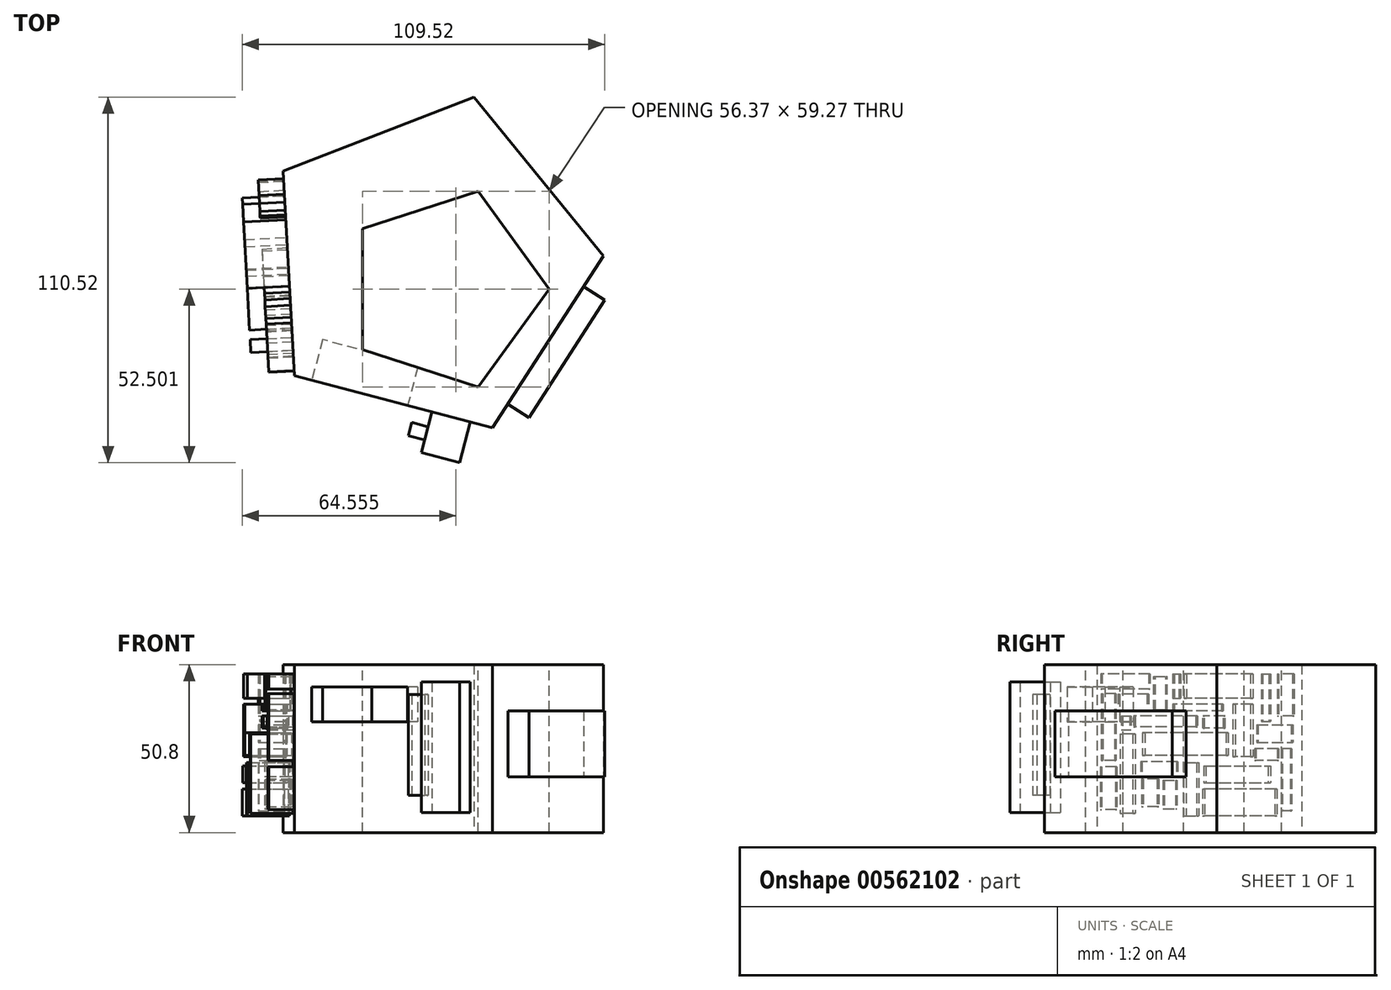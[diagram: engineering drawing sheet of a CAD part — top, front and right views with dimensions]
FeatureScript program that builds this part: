
annotation { "Feature Type Name" : "Feature", "Feature Type Description" : "" }
export const myFeature = defineFeature(function(context is Context, id is Id, definition is map)
    precondition{}
    {
        {
            var Q0;
            Q0=qCreatedBy(makeId("Top.planeOp"),FACE);
            var sketch = newSketch(context, id + "F0", { "sketchPlane" : qUnion([Q0])});
            skCircle(sketch, "E0.cCircle", {"center": v(-35.8, 17.43) * mm, "radius": 42.6 * mm, "construction": true});
            skLineSegment(sketch, "E0.0", {"start": v(16.77, 20.35) * mm, "end": v(-16.77, -31.67) * mm});
            skLineSegment(sketch, "E0.1", {"start": v(-16.77, -31.67) * mm, "end": v(-76.61, -15.84) * mm});
            skLineSegment(sketch, "E0.2", {"start": v(-76.61, -15.84) * mm, "end": v(-80.05, 45.96) * mm});
            skLineSegment(sketch, "E0.3", {"start": v(-80.05, 45.96) * mm, "end": v(-22.34, 68.33) * mm});
            skLineSegment(sketch, "E0.4", {"start": v(-22.34, 68.33) * mm, "end": v(16.77, 20.35) * mm});
            skPoint(sketch, "E0.0.midPoint", {"position": v(0, -5.66) * mm});
            skSolve(sketch);
        }
        {
            var Q0;
            Q0 = qSketchRegion(id + "F0", true);
            extrude(context, id + "F1", {"entities" : qUnion([Q0]), "depth" : 25.4 * mm, "offsetDistance" : 25.4 * mm});
        }
        {
            var Q0;
            Q0=makeQuery(id+"F1.opExtrude","CAP_FACE",FACE,{"disambiguationData":[OSD([sQuery(id+"F0.wireOp",EDGE,"E0.0"),sQuery(id+"F0.wireOp",EDGE,"E0.1"),sQuery(id+"F0.wireOp",EDGE,"E0.2"),sQuery(id+"F0.wireOp",EDGE,"E0.3"),sQuery(id+"F0.wireOp",EDGE,"E0.4")])],"isStart":true});
            extrude(context, id + "F2", {"entities" : qUnion([Q0]), "operationType" : NewBodyOperationType.ADD, "depth" : 25.4 * mm, "offsetDistance" : 25.4 * mm});
        }
        {
            var Q0;
            {var subQ0=sQuery(id+"F0.wireOp",EDGE,"E0.0");Q0=makeQuery(id+"F2.boolean.opBoolean","MERGE",FACE,{"derivedFrom":[makeQuery(id+"F1.opExtrude","SWEPT_FACE",FACE,{"disambiguationData":[OSD([subQ0])]}),makeQuery(id+"F2.opExtrude","SWEPT_FACE",FACE,{"disambiguationData":[OSD([subQ0])]})]});}
            var sketch = newSketch(context, id + "F3", { "sketchPlane" : qUnion([Q0])});
            skLineSegment(sketch, "E1.bottom", {"start": v(-27.1, 11.35) * mm, "end": v(15.17, 11.35) * mm});
            skLineSegment(sketch, "E1.top", {"start": v(-27.1, -8.59) * mm, "end": v(15.17, -8.59) * mm});
            skLineSegment(sketch, "E1.left", {"start": v(-27.1, 11.35) * mm, "end": v(-27.1, -8.59) * mm});
            skLineSegment(sketch, "E1.right", {"start": v(15.17, 11.35) * mm, "end": v(15.17, -8.59) * mm});
            skSolve(sketch);
        }
        {
            var Q0;
            Q0 = qSketchRegion(id + "F3", true);
            extrude(context, id + "F4", {"entities" : qUnion([Q0]), "operationType" : NewBodyOperationType.ADD, "depth" : 7.62 * mm, "offsetDistance" : 25.4 * mm});
        }
        {
            var Q0;
            {var subQ0=sQuery(id+"F0.wireOp",EDGE,"E0.1");Q0=makeQuery(id+"F2.boolean.opBoolean","MERGE",FACE,{"derivedFrom":[makeQuery(id+"F1.opExtrude","SWEPT_FACE",FACE,{"disambiguationData":[OSD([subQ0])]}),makeQuery(id+"F2.opExtrude","SWEPT_FACE",FACE,{"disambiguationData":[OSD([subQ0])]})]});}
            var sketch = newSketch(context, id + "F5", { "sketchPlane" : qUnion([Q0])});
            skLineSegment(sketch, "E2.bottom", {"start": v(-15, 20.12) * mm, "end": v(-26.99, 20.12) * mm});
            skLineSegment(sketch, "E2.top", {"start": v(-15, -19.39) * mm, "end": v(-26.99, -19.39) * mm});
            skLineSegment(sketch, "E2.left", {"start": v(-15, 20.12) * mm, "end": v(-15, -19.39) * mm});
            skLineSegment(sketch, "E2.right", {"start": v(-26.99, 20.12) * mm, "end": v(-26.99, -19.39) * mm});
            skSolve(sketch);
        }
        {
            var Q0;
            Q0 = qSketchRegion(id + "F5", true);
            extrude(context, id + "F6", {"entities" : qUnion([Q0]), "operationType" : NewBodyOperationType.ADD, "depth" : 12.7 * mm, "offsetDistance" : 25.4 * mm});
        }
        {
            var Q0;
            {var subQ0=sQuery(id+"F0.wireOp",EDGE,"E0.1");Q0=makeQuery(id+"F2.boolean.opBoolean","MERGE",FACE,{"derivedFrom":[makeQuery(id+"F1.opExtrude","SWEPT_FACE",FACE,{"disambiguationData":[OSD([subQ0])]}),makeQuery(id+"F2.opExtrude","SWEPT_FACE",FACE,{"disambiguationData":[OSD([subQ0])]})]});}
            var sketch = newSketch(context, id + "F7", { "sketchPlane" : qUnion([Q0])});
            skLineSegment(sketch, "E3.bottom", {"start": v(-32.68, 7.96) * mm, "end": v(-63.89, 7.96) * mm});
            skLineSegment(sketch, "E3.top", {"start": v(-32.68, 19.19) * mm, "end": v(-63.89, 19.19) * mm});
            skLineSegment(sketch, "E3.left", {"start": v(-32.68, 7.96) * mm, "end": v(-32.68, 19.19) * mm});
            skLineSegment(sketch, "E3.right", {"start": v(-63.89, 7.96) * mm, "end": v(-63.89, 19.19) * mm});
            skSolve(sketch);
        }
        {
            var Q0;
            Q0=makeQuery(id+"F7.imprint","IMPRINT",FACE,{"disambiguationData":[TD([[makeQuery(id+"F7.imprint","IMPRINT",EDGE,{"derivedFrom":sQuery(id+"F7.wireOp",EDGE,"E3.bottom")}),-1.0]])]});
            extrude(context, id + "F8", {"entities" : qUnion([Q0]), "operationType" : NewBodyOperationType.ADD, "oppositeDirection" : true, "depth" : 7.62 * mm, "offsetDistance" : 25.4 * mm});
        }
        {
            var Q0;
            {var subQ0=sQuery(id+"F0.wireOp",EDGE,"E0.1");Q0=makeQuery(id+"F2.boolean.opBoolean","MERGE",FACE,{"derivedFrom":[makeQuery(id+"F1.opExtrude","SWEPT_FACE",FACE,{"disambiguationData":[OSD([subQ0])]}),makeQuery(id+"F2.opExtrude","SWEPT_FACE",FACE,{"disambiguationData":[OSD([subQ0])]})]});}
            var sketch = newSketch(context, id + "F9", { "sketchPlane" : qUnion([Q0])});
            skLineSegment(sketch, "E4.bottom", {"start": v(-34.59, 18.6) * mm, "end": v(-64.53, 18.6) * mm});
            skLineSegment(sketch, "E4.top", {"start": v(-34.59, 8.04) * mm, "end": v(-64.53, 8.04) * mm});
            skLineSegment(sketch, "E4.left", {"start": v(-34.59, 18.6) * mm, "end": v(-34.59, 8.04) * mm});
            skLineSegment(sketch, "E4.right", {"start": v(-64.53, 18.6) * mm, "end": v(-64.53, 8.04) * mm});
            skSolve(sketch);
        }
        {
            var Q0;
            Q0=makeQuery(id+"F9.imprint","IMPRINT",FACE,{"disambiguationData":[TD([[makeQuery(id+"F9.imprint","IMPRINT",EDGE,{"derivedFrom":sQuery(id+"F9.wireOp",EDGE,"E4.bottom")}),1.0]])]});
            extrude(context, id + "F10", {"entities" : qUnion([Q0]), "operationType" : NewBodyOperationType.REMOVE, "oppositeDirection" : true, "depth" : 12.7 * mm, "offsetDistance" : 25.4 * mm});
        }
        {
            var Q0;
            Q0=makeQuery(id+"F6.opExtrude","SWEPT_FACE",FACE,{"disambiguationData":[OSD([sQuery(id+"F5.wireOp",EDGE,"E2.right")])]});
            var sketch = newSketch(context, id + "F11", { "sketchPlane" : qUnion([Q0])});
            skLineSegment(sketch, "E5.bottom", {"start": v(39.53, 16.28) * mm, "end": v(43.63, 16.28) * mm});
            skLineSegment(sketch, "E5.top", {"start": v(39.53, -14.08) * mm, "end": v(43.63, -14.08) * mm});
            skLineSegment(sketch, "E5.left", {"start": v(39.53, 16.28) * mm, "end": v(39.53, -14.08) * mm});
            skLineSegment(sketch, "E5.right", {"start": v(43.63, 16.28) * mm, "end": v(43.63, -14.08) * mm});
            skSolve(sketch);
        }
        {
            var Q0;
            Q0 = qSketchRegion(id + "F11", true);
            extrude(context, id + "F12", {"entities" : qUnion([Q0]), "operationType" : NewBodyOperationType.ADD, "depth" : 5.08 * mm, "offsetDistance" : 25.4 * mm});
        }
        {
            var Q0;
            {var subQ0=sQuery(id+"F0.wireOp",EDGE,"E0.2");Q0=makeQuery(id+"F2.boolean.opBoolean","MERGE",FACE,{"derivedFrom":[makeQuery(id+"F1.opExtrude","SWEPT_FACE",FACE,{"disambiguationData":[OSD([subQ0])]}),makeQuery(id+"F2.opExtrude","SWEPT_FACE",FACE,{"disambiguationData":[OSD([subQ0])]})]});}
            var sketch = newSketch(context, id + "F13", { "sketchPlane" : qUnion([Q0])});
            skLineSegment(sketch, "E6.bottom", {"start": v(-46.83, 22.78) * mm, "end": v(-38.12, 22.78) * mm});
            skLineSegment(sketch, "E6.top", {"start": v(-46.83, 9.33) * mm, "end": v(-38.12, 9.33) * mm});
            skLineSegment(sketch, "E6.left", {"start": v(-46.83, 22.78) * mm, "end": v(-46.83, 9.33) * mm});
            skLineSegment(sketch, "E6.right", {"start": v(-38.12, 22.78) * mm, "end": v(-38.12, 9.33) * mm});
            skLineSegment(sketch, "E7.bottom", {"start": v(-35.63, 22.61) * mm, "end": v(-15.53, 22.61) * mm});
            skLineSegment(sketch, "E7.top", {"start": v(-35.63, 15.18) * mm, "end": v(-15.53, 15.18) * mm});
            skLineSegment(sketch, "E7.left", {"start": v(-35.63, 22.61) * mm, "end": v(-35.63, 15.18) * mm});
            skLineSegment(sketch, "E7.right", {"start": v(-15.53, 22.61) * mm, "end": v(-15.53, 15.18) * mm});
            skLineSegment(sketch, "E8.bottom", {"start": v(-35.63, 13.45) * mm, "end": v(-30.3, 13.45) * mm});
            skLineSegment(sketch, "E8.top", {"start": v(-35.63, -2.42) * mm, "end": v(-30.3, -2.42) * mm});
            skLineSegment(sketch, "E8.left", {"start": v(-35.63, 13.45) * mm, "end": v(-35.63, -2.42) * mm});
            skLineSegment(sketch, "E8.right", {"start": v(-30.3, 13.45) * mm, "end": v(-30.3, -2.42) * mm});
            skLineSegment(sketch, "E9.bottom", {"start": v(-28.16, 4.72) * mm, "end": v(-2.9, 4.72) * mm});
            skLineSegment(sketch, "E9.top", {"start": v(-28.16, -2.04) * mm, "end": v(-2.9, -2.04) * mm});
            skLineSegment(sketch, "E9.left", {"start": v(-28.16, 4.72) * mm, "end": v(-28.16, -2.04) * mm});
            skLineSegment(sketch, "E9.right", {"start": v(-2.9, 4.72) * mm, "end": v(-2.9, -2.04) * mm});
            skLineSegment(sketch, "E10.bottom", {"start": v(-27.8, 13.24) * mm, "end": v(-7.88, 13.24) * mm});
            skLineSegment(sketch, "E10.top", {"start": v(-27.8, 7.32) * mm, "end": v(-7.88, 7.32) * mm});
            skLineSegment(sketch, "E10.left", {"start": v(-27.8, 13.24) * mm, "end": v(-27.8, 7.32) * mm});
            skLineSegment(sketch, "E10.right", {"start": v(-7.88, 13.24) * mm, "end": v(-7.88, 7.32) * mm});
            skLineSegment(sketch, "E11.bottom", {"start": v(-13.22, 22.64) * mm, "end": v(-7.88, 22.64) * mm});
            skLineSegment(sketch, "E11.top", {"start": v(-13.22, 15.07) * mm, "end": v(-7.88, 15.07) * mm});
            skLineSegment(sketch, "E11.left", {"start": v(-13.22, 22.64) * mm, "end": v(-13.22, 15.07) * mm});
            skLineSegment(sketch, "E11.right", {"start": v(-7.88, 22.64) * mm, "end": v(-7.88, 15.07) * mm});
            skLineSegment(sketch, "E12.bottom", {"start": v(-6.28, 23.03) * mm, "end": v(-2.55, 23.03) * mm});
            skLineSegment(sketch, "E12.top", {"start": v(-6.28, 7.76) * mm, "end": v(-2.55, 7.76) * mm});
            skLineSegment(sketch, "E12.left", {"start": v(-6.28, 23.03) * mm, "end": v(-6.28, 7.76) * mm});
            skLineSegment(sketch, "E12.right", {"start": v(-2.55, 23.03) * mm, "end": v(-2.55, 7.76) * mm});
            skLineSegment(sketch, "E13.bottom", {"start": v(0, 23.06) * mm, "end": v(3.86, 23.06) * mm});
            skLineSegment(sketch, "E13.top", {"start": v(0, 7.56) * mm, "end": v(3.86, 7.56) * mm});
            skLineSegment(sketch, "E13.left", {"start": v(0, 23.06) * mm, "end": v(0, 7.56) * mm});
            skLineSegment(sketch, "E13.right", {"start": v(3.86, 23.06) * mm, "end": v(3.86, 7.56) * mm});
            skLineSegment(sketch, "E14.bottom", {"start": v(0, 4.46) * mm, "end": v(3.86, 4.46) * mm});
            skLineSegment(sketch, "E14.top", {"start": v(0, -19.61) * mm, "end": v(3.86, -19.61) * mm});
            skLineSegment(sketch, "E14.left", {"start": v(0, 4.46) * mm, "end": v(0, -19.61) * mm});
            skLineSegment(sketch, "E14.right", {"start": v(3.86, 4.46) * mm, "end": v(3.86, -19.61) * mm});
            skLineSegment(sketch, "E15.bottom", {"start": v(-3.8, -3.83) * mm, "end": v(-13.22, -3.83) * mm});
            skLineSegment(sketch, "E15.top", {"start": v(-3.8, -10.17) * mm, "end": v(-13.22, -10.17) * mm});
            skLineSegment(sketch, "E15.left", {"start": v(-3.8, -3.83) * mm, "end": v(-3.8, -10.17) * mm});
            skLineSegment(sketch, "E15.right", {"start": v(-13.22, -3.83) * mm, "end": v(-13.22, -10.17) * mm});
            skLineSegment(sketch, "E16.bottom", {"start": v(-15.35, -4.3) * mm, "end": v(-19.27, -4.3) * mm});
            skLineSegment(sketch, "E16.top", {"start": v(-15.35, -20.32) * mm, "end": v(-19.27, -20.32) * mm});
            skLineSegment(sketch, "E16.left", {"start": v(-15.35, -4.3) * mm, "end": v(-15.35, -20.32) * mm});
            skLineSegment(sketch, "E16.right", {"start": v(-19.27, -4.3) * mm, "end": v(-19.27, -20.32) * mm});
            skLineSegment(sketch, "E17.bottom", {"start": v(-3.26, -12.21) * mm, "end": v(-7.88, -12.21) * mm});
            skLineSegment(sketch, "E17.top", {"start": v(-3.26, -22.37) * mm, "end": v(-7.88, -22.37) * mm});
            skLineSegment(sketch, "E17.left", {"start": v(-3.26, -12.21) * mm, "end": v(-3.26, -22.37) * mm});
            skLineSegment(sketch, "E17.right", {"start": v(-7.88, -12.21) * mm, "end": v(-7.88, -22.37) * mm});
            skLineSegment(sketch, "E18.bottom", {"start": v(-10.73, -12.21) * mm, "end": v(-13.75, -12.21) * mm});
            skLineSegment(sketch, "E18.top", {"start": v(-10.73, -21.76) * mm, "end": v(-13.75, -21.76) * mm});
            skLineSegment(sketch, "E18.left", {"start": v(-10.73, -12.21) * mm, "end": v(-10.73, -21.76) * mm});
            skLineSegment(sketch, "E18.right", {"start": v(-13.75, -12.21) * mm, "end": v(-13.75, -21.76) * mm});
            skLineSegment(sketch, "E19.bottom", {"start": v(-21.4, -5.29) * mm, "end": v(-40.96, -5.29) * mm});
            skLineSegment(sketch, "E19.top", {"start": v(-21.4, -10.27) * mm, "end": v(-40.96, -10.27) * mm});
            skLineSegment(sketch, "E19.left", {"start": v(-21.4, -5.29) * mm, "end": v(-21.4, -10.27) * mm});
            skLineSegment(sketch, "E19.right", {"start": v(-40.96, -5.29) * mm, "end": v(-40.96, -10.27) * mm});
            skLineSegment(sketch, "E20.bottom", {"start": v(-38.3, 7.56) * mm, "end": v(-42.92, 7.56) * mm});
            skLineSegment(sketch, "E20.top", {"start": v(-38.3, -3.72) * mm, "end": v(-42.92, -3.72) * mm});
            skLineSegment(sketch, "E20.left", {"start": v(-38.3, 7.56) * mm, "end": v(-38.3, -3.72) * mm});
            skLineSegment(sketch, "E20.right", {"start": v(-42.92, 7.56) * mm, "end": v(-42.92, -3.72) * mm});
            skLineSegment(sketch, "E21.bottom", {"start": v(-44.7, 7.56) * mm, "end": v(-47.72, 7.56) * mm});
            skLineSegment(sketch, "E21.top", {"start": v(-44.7, -21.71) * mm, "end": v(-47.72, -21.71) * mm});
            skLineSegment(sketch, "E21.left", {"start": v(-44.7, 7.56) * mm, "end": v(-44.7, -21.71) * mm});
            skLineSegment(sketch, "E21.right", {"start": v(-47.72, 7.56) * mm, "end": v(-47.72, -21.71) * mm});
            skLineSegment(sketch, "E22.bottom", {"start": v(-42.92, -12.21) * mm, "end": v(-21.04, -12.21) * mm});
            skLineSegment(sketch, "E22.top", {"start": v(-42.92, -20.32) * mm, "end": v(-21.04, -20.32) * mm});
            skLineSegment(sketch, "E22.left", {"start": v(-42.92, -12.21) * mm, "end": v(-42.92, -20.32) * mm});
            skLineSegment(sketch, "E22.right", {"start": v(-21.04, -12.21) * mm, "end": v(-21.04, -20.32) * mm});
            skLineSegment(sketch, "E23.bottom", {"start": v(3.86, 23.06) * mm, "end": v(8.66, 23.06) * mm});
            skLineSegment(sketch, "E23.top", {"start": v(3.86, -20.32) * mm, "end": v(8.66, -20.32) * mm});
            skLineSegment(sketch, "E23.left", {"start": v(3.86, 23.06) * mm, "end": v(3.86, -20.32) * mm});
            skLineSegment(sketch, "E23.right", {"start": v(8.66, 23.06) * mm, "end": v(8.66, -20.32) * mm});
            skSolve(sketch);
        }
        {
            var Q0;
            Q0=makeQuery(id+"F13.imprint","IMPRINT",FACE,{"disambiguationData":[TD([[makeQuery(id+"F13.imprint","IMPRINT",EDGE,{"derivedFrom":sQuery(id+"F13.wireOp",EDGE,"E7.bottom")}),-1.0]])]});
            var Q1;
            Q1=makeQuery(id+"F13.imprint","IMPRINT",FACE,{"disambiguationData":[TD([[makeQuery(id+"F13.imprint","IMPRINT",EDGE,{"derivedFrom":sQuery(id+"F13.wireOp",EDGE,"E8.bottom")}),-1.0]])]});
            var Q2;
            Q2=makeQuery(id+"F13.imprint","IMPRINT",FACE,{"disambiguationData":[TD([[makeQuery(id+"F13.imprint","IMPRINT",EDGE,{"derivedFrom":sQuery(id+"F13.wireOp",EDGE,"E9.bottom")}),-1.0]])]});
            var Q3;
            Q3=makeQuery(id+"F13.imprint","IMPRINT",FACE,{"disambiguationData":[TD([[makeQuery(id+"F13.imprint","IMPRINT",EDGE,{"derivedFrom":sQuery(id+"F13.wireOp",EDGE,"E16.bottom")}),1.0]])]});
            var Q4;
            Q4=makeQuery(id+"F13.imprint","IMPRINT",FACE,{"disambiguationData":[TD([[makeQuery(id+"F13.imprint","IMPRINT",EDGE,{"derivedFrom":sQuery(id+"F13.wireOp",EDGE,"E19.bottom")}),1.0]])]});
            var Q5;
            Q5=makeQuery(id+"F13.imprint","IMPRINT",FACE,{"disambiguationData":[TD([[makeQuery(id+"F13.imprint","IMPRINT",EDGE,{"derivedFrom":sQuery(id+"F13.wireOp",EDGE,"E22.bottom")}),-1.0]])]});
            var Q6;
            {var subQ0=sQuery(id+"F13.wireOp",EDGE,"E14.bottom");Q6=makeQuery(id+"F13.imprint","IMPRINT",FACE,{"disambiguationData":[TD([[makeQuery(id+"F13.imprint","IMPRINT",EDGE,{"derivedFrom":subQ0}),-1.0]])]});}
            extrude(context, id + "F14", {"entities" : qUnion([Q0, Q1, Q2, Q3, Q4, Q5, Q6]), "operationType" : NewBodyOperationType.ADD, "depth" : 12.7 * mm, "offsetDistance" : 25.4 * mm});
        }
        {
            var Q0;
            {var subQ0=sQuery(id+"F0.wireOp",EDGE,"E0.2");Q0=makeQuery(id+"F2.boolean.opBoolean","MERGE",FACE,{"derivedFrom":[makeQuery(id+"F1.opExtrude","SWEPT_FACE",FACE,{"disambiguationData":[OSD([subQ0])]}),makeQuery(id+"F2.opExtrude","SWEPT_FACE",FACE,{"disambiguationData":[OSD([subQ0])]})]});}
            var sketch = newSketch(context, id + "F15", { "sketchPlane" : qUnion([Q0])});
            skLineSegment(sketch, "E24.bottom", {"start": v(-38.59, 22.51) * mm, "end": v(-40.93, 22.51) * mm});
            skLineSegment(sketch, "E24.top", {"start": v(-38.59, 8.16) * mm, "end": v(-40.93, 8.16) * mm});
            skLineSegment(sketch, "E24.left", {"start": v(-38.59, 22.51) * mm, "end": v(-38.59, 8.16) * mm});
            skLineSegment(sketch, "E24.right", {"start": v(-40.93, 22.51) * mm, "end": v(-40.93, 8.16) * mm});
            skLineSegment(sketch, "E25.bottom", {"start": v(-37.16, 7.25) * mm, "end": v(-47.66, 7.25) * mm});
            skLineSegment(sketch, "E25.top", {"start": v(-37.16, 1.86) * mm, "end": v(-47.66, 1.86) * mm});
            skLineSegment(sketch, "E25.left", {"start": v(-37.16, 7.25) * mm, "end": v(-37.16, 1.86) * mm});
            skLineSegment(sketch, "E25.right", {"start": v(-47.66, 7.25) * mm, "end": v(-47.66, 1.86) * mm});
            skLineSegment(sketch, "E26.bottom", {"start": v(-48.07, 22.61) * mm, "end": v(-43.38, 22.61) * mm});
            skLineSegment(sketch, "E26.top", {"start": v(-48.07, 9.9) * mm, "end": v(-43.38, 9.9) * mm});
            skLineSegment(sketch, "E26.left", {"start": v(-48.07, 22.61) * mm, "end": v(-48.07, 9.9) * mm});
            skLineSegment(sketch, "E26.right", {"start": v(-43.38, 22.61) * mm, "end": v(-43.38, 9.9) * mm});
            skLineSegment(sketch, "E27.bottom", {"start": v(-47.35, 0) * mm, "end": v(-44.6, 0) * mm});
            skLineSegment(sketch, "E27.top", {"start": v(-47.35, -18.8) * mm, "end": v(-44.6, -18.8) * mm});
            skLineSegment(sketch, "E27.left", {"start": v(-47.35, 0) * mm, "end": v(-47.35, -18.8) * mm});
            skLineSegment(sketch, "E27.right", {"start": v(-44.6, 0) * mm, "end": v(-44.6, -18.8) * mm});
            skLineSegment(sketch, "E28.bottom", {"start": v(-43.38, 0) * mm, "end": v(-36.55, 0) * mm});
            skLineSegment(sketch, "E28.top", {"start": v(-43.38, -3.64) * mm, "end": v(-36.55, -3.64) * mm});
            skLineSegment(sketch, "E28.left", {"start": v(-43.38, 0) * mm, "end": v(-43.38, -3.64) * mm});
            skLineSegment(sketch, "E28.right", {"start": v(-36.55, 0) * mm, "end": v(-36.55, -3.64) * mm});
            skLineSegment(sketch, "E29.bottom", {"start": v(-12.9, -4.05) * mm, "end": v(-2.1, -4.05) * mm});
            skLineSegment(sketch, "E29.top", {"start": v(-12.9, -8.42) * mm, "end": v(-2.1, -8.42) * mm});
            skLineSegment(sketch, "E29.left", {"start": v(-12.9, -4.05) * mm, "end": v(-12.9, -8.42) * mm});
            skLineSegment(sketch, "E29.right", {"start": v(-2.1, -4.05) * mm, "end": v(-2.1, -8.42) * mm});
            skLineSegment(sketch, "E30.bottom", {"start": v(-7.1, -9.24) * mm, "end": v(-2.41, -9.24) * mm});
            skLineSegment(sketch, "E30.top", {"start": v(-7.1, -17.58) * mm, "end": v(-2.41, -17.58) * mm});
            skLineSegment(sketch, "E30.left", {"start": v(-7.1, -9.24) * mm, "end": v(-7.1, -17.58) * mm});
            skLineSegment(sketch, "E30.right", {"start": v(-2.41, -9.24) * mm, "end": v(-2.41, -17.58) * mm});
            skLineSegment(sketch, "E31.bottom", {"start": v(-8.83, -9.54) * mm, "end": v(-12.6, -9.54) * mm});
            skLineSegment(sketch, "E31.top", {"start": v(-8.83, -18.2) * mm, "end": v(-12.6, -18.2) * mm});
            skLineSegment(sketch, "E31.left", {"start": v(-8.83, -9.54) * mm, "end": v(-8.83, -18.2) * mm});
            skLineSegment(sketch, "E31.right", {"start": v(-12.6, -9.54) * mm, "end": v(-12.6, -18.2) * mm});
            skLineSegment(sketch, "E32.bottom", {"start": v(-27.18, 6.23) * mm, "end": v(-20.96, 6.23) * mm});
            skLineSegment(sketch, "E32.top", {"start": v(-27.18, 9.9) * mm, "end": v(-20.96, 9.9) * mm});
            skLineSegment(sketch, "E32.left", {"start": v(-27.18, 6.23) * mm, "end": v(-27.18, 9.9) * mm});
            skLineSegment(sketch, "E32.right", {"start": v(-20.96, 6.23) * mm, "end": v(-20.96, 9.9) * mm});
            skLineSegment(sketch, "E33.bottom", {"start": v(-26.56, 13.45) * mm, "end": v(-11.79, 13.45) * mm});
            skLineSegment(sketch, "E33.top", {"start": v(-26.56, 11.32) * mm, "end": v(-11.79, 11.32) * mm});
            skLineSegment(sketch, "E33.left", {"start": v(-26.56, 13.45) * mm, "end": v(-26.56, 11.32) * mm});
            skLineSegment(sketch, "E33.right", {"start": v(-11.79, 13.45) * mm, "end": v(-11.79, 11.32) * mm});
            skLineSegment(sketch, "E34.bottom", {"start": v(-18.82, 9.9) * mm, "end": v(0, 9.9) * mm});
            skLineSegment(sketch, "E34.top", {"start": v(-18.82, 6.54) * mm, "end": v(0, 6.54) * mm});
            skLineSegment(sketch, "E34.left", {"start": v(-18.82, 9.9) * mm, "end": v(-18.82, 6.54) * mm});
            skLineSegment(sketch, "E34.right", {"start": v(0, 9.9) * mm, "end": v(0, 6.54) * mm});
            skLineSegment(sketch, "E35.bottom", {"start": v(-6.08, 11.73) * mm, "end": v(-9.75, 11.73) * mm});
            skLineSegment(sketch, "E35.top", {"start": v(-6.08, 21.8) * mm, "end": v(-9.75, 21.8) * mm});
            skLineSegment(sketch, "E35.left", {"start": v(-6.08, 11.73) * mm, "end": v(-6.08, 21.8) * mm});
            skLineSegment(sketch, "E35.right", {"start": v(-9.75, 11.73) * mm, "end": v(-9.75, 21.8) * mm});
            skLineSegment(sketch, "E36.bottom", {"start": v(-11.79, 22.61) * mm, "end": v(-13.72, 22.61) * mm});
            skLineSegment(sketch, "E36.top", {"start": v(-11.79, 15.18) * mm, "end": v(-13.72, 15.18) * mm});
            skLineSegment(sketch, "E36.left", {"start": v(-11.79, 22.61) * mm, "end": v(-11.79, 15.18) * mm});
            skLineSegment(sketch, "E36.right", {"start": v(-13.72, 22.61) * mm, "end": v(-13.72, 15.18) * mm});
            skLineSegment(sketch, "E37.bottom", {"start": v(-4.45, 22.61) * mm, "end": v(10.02, 22.61) * mm});
            skLineSegment(sketch, "E37.top", {"start": v(-4.45, 18.03) * mm, "end": v(10.02, 18.03) * mm});
            skLineSegment(sketch, "E37.left", {"start": v(-4.45, 22.61) * mm, "end": v(-4.45, 18.03) * mm});
            skLineSegment(sketch, "E37.right", {"start": v(10.02, 22.61) * mm, "end": v(10.02, 18.03) * mm});
            skLineSegment(sketch, "E38.bottom", {"start": v(-4.04, 16.4) * mm, "end": v(4.72, 16.4) * mm});
            skLineSegment(sketch, "E38.top", {"start": v(-4.04, 11.52) * mm, "end": v(4.72, 11.52) * mm});
            skLineSegment(sketch, "E38.left", {"start": v(-4.04, 16.4) * mm, "end": v(-4.04, 11.52) * mm});
            skLineSegment(sketch, "E38.right", {"start": v(4.72, 16.4) * mm, "end": v(4.72, 11.52) * mm});
            skLineSegment(sketch, "E39.bottom", {"start": v(5.84, 16.6) * mm, "end": v(9.82, 16.6) * mm});
            skLineSegment(sketch, "E39.top", {"start": v(5.84, -3.64) * mm, "end": v(9.82, -3.64) * mm});
            skLineSegment(sketch, "E39.left", {"start": v(5.84, 16.6) * mm, "end": v(5.84, -3.64) * mm});
            skLineSegment(sketch, "E39.right", {"start": v(9.82, 16.6) * mm, "end": v(9.82, -3.64) * mm});
            skLineSegment(sketch, "E40.bottom", {"start": v(3.8, 9.9) * mm, "end": v(1.26, 9.9) * mm});
            skLineSegment(sketch, "E40.top", {"start": v(3.8, 5.72) * mm, "end": v(1.26, 5.72) * mm});
            skLineSegment(sketch, "E40.left", {"start": v(3.8, 9.9) * mm, "end": v(3.8, 5.72) * mm});
            skLineSegment(sketch, "E40.right", {"start": v(1.26, 9.9) * mm, "end": v(1.26, 5.72) * mm});
            skLineSegment(sketch, "E41.bottom", {"start": v(5.54, -5.47) * mm, "end": v(10.12, -5.47) * mm});
            skLineSegment(sketch, "E41.top", {"start": v(5.54, -18.5) * mm, "end": v(10.12, -18.5) * mm});
            skLineSegment(sketch, "E41.left", {"start": v(5.54, -5.47) * mm, "end": v(5.54, -18.5) * mm});
            skLineSegment(sketch, "E41.right", {"start": v(10.12, -5.47) * mm, "end": v(10.12, -18.5) * mm});
            skSolve(sketch);
        }
        {
            var Q0;
            Q0 = qSketchRegion(id + "F15", true);
            extrude(context, id + "F16", {"entities" : qUnion([Q0]), "operationType" : NewBodyOperationType.ADD, "depth" : 7.62 * mm, "offsetDistance" : 25.4 * mm});
        }
        {
            var Q0;
            {var subQ0=sQuery(id+"F0.wireOp",EDGE,"E0.2");Q0=makeQuery(id+"F2.boolean.opBoolean","MERGE",FACE,{"derivedFrom":[makeQuery(id+"F1.opExtrude","SWEPT_FACE",FACE,{"disambiguationData":[OSD([subQ0])]}),makeQuery(id+"F2.opExtrude","SWEPT_FACE",FACE,{"disambiguationData":[OSD([subQ0])]})]});}
            var sketch = newSketch(context, id + "F17", { "sketchPlane" : qUnion([Q0])});
            skSolve(sketch);
        }
        {
            var Q0;
            Q0 = qSketchRegion(id + "F17", true);
            var Q1;
            {var subQ1=sQuery(id+"F0.wireOp",EDGE,"E0.2");Q1=makeQuery(id+"F17.imprint","IMPRINT",FACE,{"disambiguationData":[TD([[makeQuery(id+"F17.imprint","IMPRINT",EDGE,{"derivedFrom":makeQuery(id+"F1.opExtrude","CAP_EDGE",EDGE,{"disambiguationData":[OSD([subQ1])],"isStart":false})}),1.0]])]});}
            extrude(context, id + "F18", {"entities" : qUnion([Q0, Q1]), "operationType" : NewBodyOperationType.REMOVE, "oppositeDirection" : true, "depth" : 5.08 * mm, "offsetDistance" : 25.4 * mm});
        }
        {
            var Q0;
            Q0=makeQuery(id+"F1.opExtrude","CAP_FACE",FACE,{"disambiguationData":[OSD([sQuery(id+"F0.wireOp",EDGE,"E0.0"),sQuery(id+"F0.wireOp",EDGE,"E0.1"),sQuery(id+"F0.wireOp",EDGE,"E0.2"),sQuery(id+"F0.wireOp",EDGE,"E0.3"),sQuery(id+"F0.wireOp",EDGE,"E0.4")])],"isStart":false});
            var sketch = newSketch(context, id + "F19", { "sketchPlane" : qUnion([Q0])});
            skCircle(sketch, "E42.cCircle", {"center": v(-30.74, 10.31) * mm, "radius": 25.2 * mm, "construction": true});
            skLineSegment(sketch, "E42.0", {"start": v(-55.95, -8) * mm, "end": v(-55.95, 28.63) * mm});
            skLineSegment(sketch, "E42.1", {"start": v(-55.95, 28.63) * mm, "end": v(-21.11, 39.94) * mm});
            skLineSegment(sketch, "E42.2", {"start": v(-21.11, 39.94) * mm, "end": v(0.42, 10.31) * mm});
            skLineSegment(sketch, "E42.3", {"start": v(0.42, 10.31) * mm, "end": v(-21.11, -19.32) * mm});
            skLineSegment(sketch, "E42.4", {"start": v(-21.11, -19.32) * mm, "end": v(-55.95, -8) * mm});
            skPoint(sketch, "E42.0.midPoint", {"position": v(-55.95, 10.31) * mm});
            skSolve(sketch);
        }
        {
            var Q0;
            Q0 = qSketchRegion(id + "F19", true);
            extrude(context, id + "F20", {"entities" : qUnion([Q0]), "operationType" : NewBodyOperationType.REMOVE, "oppositeDirection" : true, "depth" : 76.2 * mm, "offsetDistance" : 25.4 * mm});
        }
        {
            var Q0;
            Q0=makeQuery(id+"F18.boolean.opBoolean","COPY",FACE,{"derivedFrom":makeQuery(id+"F18.opExtrude","CAP_FACE",FACE,{"disambiguationData":[OSD([sQuery(id+"F0.wireOp",EDGE,"E0.1"),sQuery(id+"F0.wireOp",EDGE,"E0.2"),sQuery(id+"F0.wireOp",EDGE,"E0.3"),sQuery(id+"F13.wireOp",EDGE,"E7.bottom"),sQuery(id+"F13.wireOp",EDGE,"E7.top"),sQuery(id+"F13.wireOp",EDGE,"E7.left"),sQuery(id+"F13.wireOp",EDGE,"E7.right"),sQuery(id+"F13.wireOp",EDGE,"E8.bottom"),sQuery(id+"F13.wireOp",EDGE,"E8.top"),sQuery(id+"F13.wireOp",EDGE,"E8.left"),sQuery(id+"F13.wireOp",EDGE,"E8.right"),sQuery(id+"F13.wireOp",EDGE,"E9.bottom"),sQuery(id+"F13.wireOp",EDGE,"E9.top"),sQuery(id+"F13.wireOp",EDGE,"E9.left"),sQuery(id+"F13.wireOp",EDGE,"E9.right"),sQuery(id+"F13.wireOp",EDGE,"E14.bottom"),sQuery(id+"F13.wireOp",EDGE,"E14.top"),sQuery(id+"F13.wireOp",EDGE,"E14.left"),sQuery(id+"F13.wireOp",EDGE,"E16.bottom"),sQuery(id+"F13.wireOp",EDGE,"E16.top"),sQuery(id+"F13.wireOp",EDGE,"E16.left"),sQuery(id+"F13.wireOp",EDGE,"E16.right"),sQuery(id+"F13.wireOp",EDGE,"E19.bottom"),sQuery(id+"F13.wireOp",EDGE,"E19.top"),sQuery(id+"F13.wireOp",EDGE,"E19.left"),sQuery(id+"F13.wireOp",EDGE,"E19.right"),sQuery(id+"F13.wireOp",EDGE,"E22.bottom"),sQuery(id+"F13.wireOp",EDGE,"E22.top"),sQuery(id+"F13.wireOp",EDGE,"E22.left"),sQuery(id+"F13.wireOp",EDGE,"E22.right"),sQuery(id+"F13.wireOp",EDGE,"E23.left"),sQuery(id+"F15.wireOp",EDGE,"E24.bottom"),sQuery(id+"F15.wireOp",EDGE,"E24.top"),sQuery(id+"F15.wireOp",EDGE,"E24.left"),sQuery(id+"F15.wireOp",EDGE,"E24.right"),sQuery(id+"F15.wireOp",EDGE,"E25.bottom"),sQuery(id+"F15.wireOp",EDGE,"E25.top"),sQuery(id+"F15.wireOp",EDGE,"E25.left"),sQuery(id+"F15.wireOp",EDGE,"E25.right"),sQuery(id+"F15.wireOp",EDGE,"E26.bottom"),sQuery(id+"F15.wireOp",EDGE,"E26.top"),sQuery(id+"F15.wireOp",EDGE,"E26.left"),sQuery(id+"F15.wireOp",EDGE,"E26.right"),sQuery(id+"F15.wireOp",EDGE,"E27.bottom"),sQuery(id+"F15.wireOp",EDGE,"E27.top"),sQuery(id+"F15.wireOp",EDGE,"E27.left"),sQuery(id+"F15.wireOp",EDGE,"E27.right"),sQuery(id+"F15.wireOp",EDGE,"E28.bottom"),sQuery(id+"F15.wireOp",EDGE,"E28.top"),sQuery(id+"F15.wireOp",EDGE,"E28.left"),sQuery(id+"F15.wireOp",EDGE,"E28.right"),sQuery(id+"F15.wireOp",EDGE,"E29.bottom"),sQuery(id+"F15.wireOp",EDGE,"E29.top"),sQuery(id+"F15.wireOp",EDGE,"E29.left"),sQuery(id+"F15.wireOp",EDGE,"E29.right"),sQuery(id+"F15.wireOp",EDGE,"E30.bottom"),sQuery(id+"F15.wireOp",EDGE,"E30.top"),sQuery(id+"F15.wireOp",EDGE,"E30.left"),sQuery(id+"F15.wireOp",EDGE,"E30.right"),sQuery(id+"F15.wireOp",EDGE,"E31.bottom"),sQuery(id+"F15.wireOp",EDGE,"E31.top"),sQuery(id+"F15.wireOp",EDGE,"E31.left"),sQuery(id+"F15.wireOp",EDGE,"E31.right"),sQuery(id+"F15.wireOp",EDGE,"E32.bottom"),sQuery(id+"F15.wireOp",EDGE,"E32.top"),sQuery(id+"F15.wireOp",EDGE,"E32.left"),sQuery(id+"F15.wireOp",EDGE,"E32.right"),sQuery(id+"F15.wireOp",EDGE,"E33.bottom"),sQuery(id+"F15.wireOp",EDGE,"E33.top"),sQuery(id+"F15.wireOp",EDGE,"E33.left"),sQuery(id+"F15.wireOp",EDGE,"E33.right"),sQuery(id+"F15.wireOp",EDGE,"E34.bottom"),sQuery(id+"F15.wireOp",EDGE,"E34.top"),sQuery(id+"F15.wireOp",EDGE,"E34.left"),sQuery(id+"F15.wireOp",EDGE,"E34.right"),sQuery(id+"F15.wireOp",EDGE,"E35.bottom"),sQuery(id+"F15.wireOp",EDGE,"E35.top"),sQuery(id+"F15.wireOp",EDGE,"E35.left"),sQuery(id+"F15.wireOp",EDGE,"E35.right"),sQuery(id+"F15.wireOp",EDGE,"E36.bottom"),sQuery(id+"F15.wireOp",EDGE,"E36.top"),sQuery(id+"F15.wireOp",EDGE,"E36.left"),sQuery(id+"F15.wireOp",EDGE,"E36.right"),sQuery(id+"F15.wireOp",EDGE,"E37.bottom"),sQuery(id+"F15.wireOp",EDGE,"E37.top"),sQuery(id+"F15.wireOp",EDGE,"E37.left"),sQuery(id+"F15.wireOp",EDGE,"E37.right"),sQuery(id+"F15.wireOp",EDGE,"E38.bottom"),sQuery(id+"F15.wireOp",EDGE,"E38.top"),sQuery(id+"F15.wireOp",EDGE,"E38.left"),sQuery(id+"F15.wireOp",EDGE,"E38.right"),sQuery(id+"F15.wireOp",EDGE,"E39.bottom"),sQuery(id+"F15.wireOp",EDGE,"E39.top"),sQuery(id+"F15.wireOp",EDGE,"E39.left"),sQuery(id+"F15.wireOp",EDGE,"E39.right"),sQuery(id+"F15.wireOp",EDGE,"E40.bottom"),sQuery(id+"F15.wireOp",EDGE,"E40.top"),sQuery(id+"F15.wireOp",EDGE,"E40.left"),sQuery(id+"F15.wireOp",EDGE,"E40.right"),sQuery(id+"F15.wireOp",EDGE,"E41.bottom"),sQuery(id+"F15.wireOp",EDGE,"E41.top"),sQuery(id+"F15.wireOp",EDGE,"E41.left"),sQuery(id+"F15.wireOp",EDGE,"E41.right")])],"isStart":false})});
            extrude(context, id + "F21", {"entities" : qUnion([Q0]), "operationType" : NewBodyOperationType.ADD, "depth" : 5.08 * mm, "offsetDistance" : 25.4 * mm});
        }
    });
